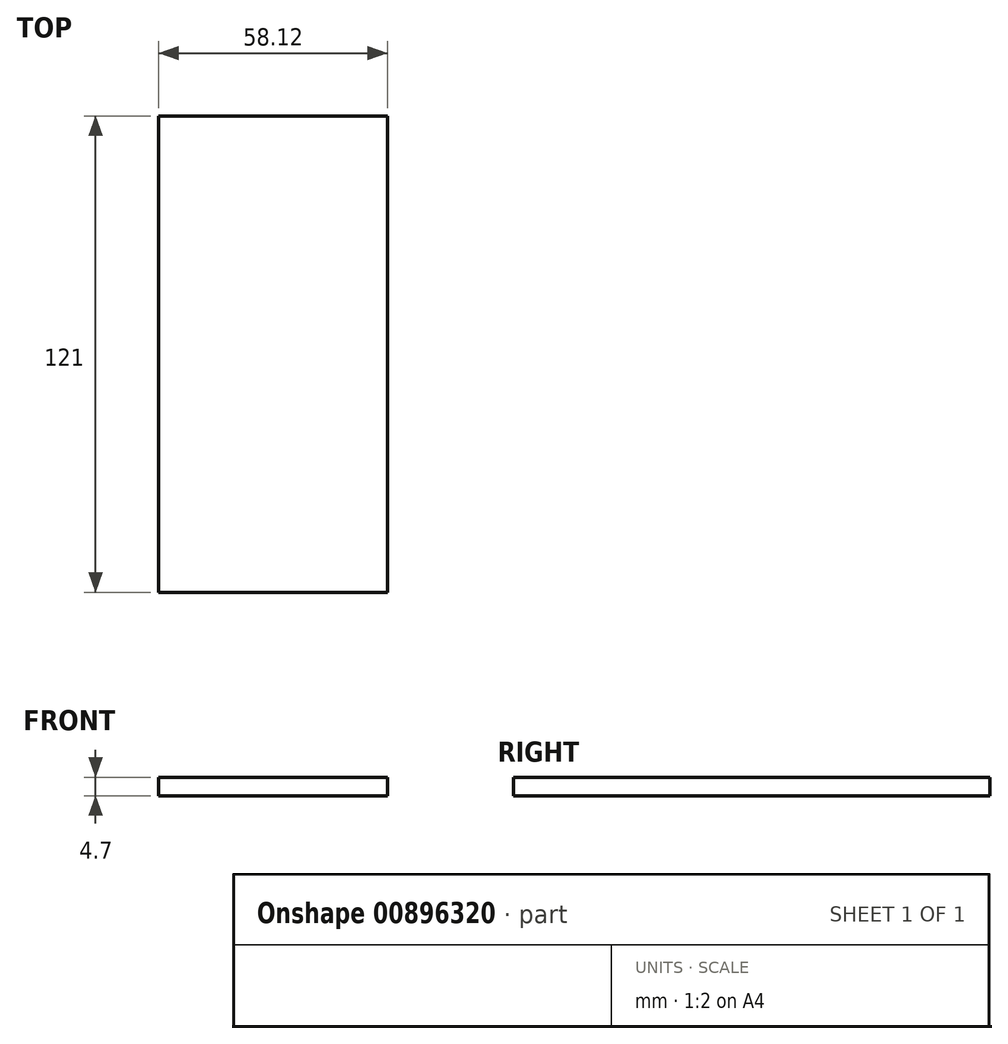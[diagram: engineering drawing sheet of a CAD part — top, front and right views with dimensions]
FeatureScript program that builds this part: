
annotation { "Feature Type Name" : "Feature", "Feature Type Description" : "" }
export const myFeature = defineFeature(function(context is Context, id is Id, definition is map)
    precondition{}
    {
        {
            var Q0;
            Q0=qCreatedBy(makeId("Top.planeOp"),FACE);
            var sketch = newSketch(context, id + "F0", { "sketchPlane" : qUnion([Q0])});
            skLineSegment(sketch, "E0.bottom", {"start": v(-29.06, 60.5) * mm, "end": v(29.06, 60.5) * mm});
            skLineSegment(sketch, "E0.top", {"start": v(-29.06, -60.5) * mm, "end": v(29.06, -60.5) * mm});
            skLineSegment(sketch, "E0.left", {"start": v(-29.06, 60.5) * mm, "end": v(-29.06, -60.5) * mm});
            skLineSegment(sketch, "E0.right", {"start": v(29.06, 60.5) * mm, "end": v(29.06, -60.5) * mm});
            skPoint(sketch, "E0.middle", {"position": v(0, 0) * mm});
            skSolve(sketch);
        }
        {
            var Q0;
            Q0=makeQuery(id+"F0.imprint","IMPRINT",FACE,{"disambiguationData":[TD([[makeQuery(id+"F0.imprint","IMPRINT",EDGE,{"derivedFrom":sQuery(id+"F0.wireOp",EDGE,"E0.bottom")}),-1.0]])]});
            extrude(context, id + "F1", {"entities" : qUnion([Q0]), "depth" : 4.7 * mm, "offsetDistance" : 25 * mm});
        }
    });
